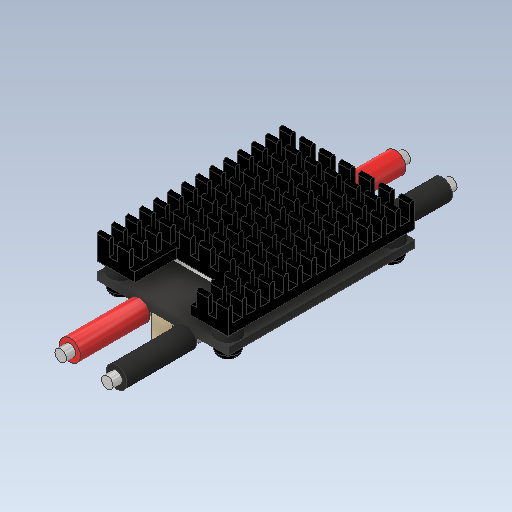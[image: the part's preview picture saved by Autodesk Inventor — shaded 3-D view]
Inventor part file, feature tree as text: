
AUTODESK INVENTOR PART (.ipt)
format: ipt  version: 2020.1 (Build 241239000, 239)  size: 1,061,888 bytes
history: native  units: mm
features: extrude x16, sketch x13, mirror x6, fillet x4, pattern_linear x2, plane x1, revolve x1, chamfer x1, emboss x1, projected_geometry x1
ambient origin geometry x8: Origin, YZ Plane, XZ Plane, XY Plane, X Axis, Y Axis, Z Axis, Center Point
bodies: Solid1 (feature_tree)
feature tree (46):
  extrude  "Extrusion1"  Depth=40.0mm
  extrude  "Extrusion2"  Depth=5.0mm
  extrude  "Extrusion3"  Depth=9.0mm
  extrude  "Extrusion4"  Depth=8.0mm
  extrude  "Extrusion5"  Depth=1.0mm TaperAngle=0.0deg
  fillet  "Fillet1"  Radius=0.2mm
  pattern_linear  "Rectangular Pattern1"  Count1=14 Spacing1=3.0mm
  mirror  "Mirror1"
  extrude  "Extrusion6"  Depth=1.0mm
  fillet  "Fillet2"  Radius=1.0mm
  pattern_linear  "Rectangular Pattern2"  Count1=11 Spacing1=3.0mm
  extrude  "Extrusion7"  Depth=0.1mm TaperAngle=0.0deg
  fillet  "Fillet3"  Radius=1.0mm
  extrude  "Extrusion8"  Depth=1.0mm
  mirror  "Mirror2"
  mirror  "Mirror3"
  sketch  "Sketch9"  dims[d19=0.5mm d20=140.0mm d22=3.0mm]
  extrude  "Extrusion9"  Depth=0.1mm
  fillet  "Fillet4"  Radius=1.0mm
  mirror  "Mirror4"
  plane  "Work Plane1"
  revolve  "Revolution1"  [1 undecoded]
  mirror  "Mirror5"
  mirror  "Mirror6"
  extrude  "Extrusion10"  Depth=0.1mm
  extrude  "Extrusion11"  Depth=0.1mm
  extrude  "Extrusion12"  Depth=0.1mm
  extrude  "Extrusion13"  Depth=0.1mm
  extrude  "Extrusion14"  Depth=0.1mm
  chamfer  "Chamfer1"  Distance=0.1mm
  extrude  "Extrusion15"  Depth=0.1mm
  extrude  "Extrusion16"  Depth=0.1mm TaperAngle=0.0deg
  emboss  "Emboss1"
  sketch  "Sketch1"  dims[d0=28.0mm d1=40.0mm]
  sketch  "Sketch2"  dims[d2=1.57mm d3=0.0mm d4=5.0mm]
  sketch  "Sketch3"  dims[d5=2.0mm d6=0.0mm d7=9.0mm]
  sketch  "Sketch4"  dims[d8=8.0mm d9=8.0mm]
  projected_geometry  "Projected Loop1"
  sketch  "Sketch5"  dims[d10=2.0mm d11=0.0mm d12=1.0mm d13=0.0mm d14=0.2mm]
  sketch  "Sketch6"  dims[d15=1.0mm]
  sketch  "Sketch7"  dims[d16=2.5mm]
  sketch  "Sketch8"  dims[d17=3.5mm d18=0.0mm]
  sketch  "Sketch10"  dims[d23=20.0mm d25=4.25mm d26=2.5mm d27=1.0mm]
  sketch  "Sketch11"  dims[d28=3.5mm d29=0.0mm]
  sketch  "Sketch12"  dims[d30=0.5mm d31=110.0mm d33=3.0mm d34=30.0mm d36=4.25mm]
  sketch  "Sketch13"  dims[d37=4.5mm d38=2.0mm d39=0.0mm d40=1.0mm d41=1.0mm d42=4.0mm d43=1.0mm d44=1.5mm d45=0.0mm d46=5.0mm d47=8.0mm d48=0.1mm d49=6.0mm d50=4.0mm d51=0.1mm d52=0.5mm d53=3.0mm d54=0.0mm d55=1.999992mm d59=1.24mm d60=2.0mm d61=20.0mm d62=90.0deg d63=2.25mm d64=0.5mm d65=1.0mm d66=1.0mm d67=0.5mm d68=0.5mm d70=0.3mm d71=0.5mm d72=0.5mm d73=0.5mm d74=0.5mm d75=1.48mm d76=1.0mm d77=0.0mm d78=6.0mm d79=0.0mm d80=4.0mm d81=0.0mm d82=1.5mm d83=0.0mm d84=5.0mm d85=0.0mm d86=0.2mm d87=2.0mm d88=45.0deg d89=0.5mm d90=0.5mm d91=1.0mm d92=6.0mm d93=0.0mm d94=1.0mm d95=2.0mm d97=0.5mm d98=2.0mm d99=6.0mm d100=0.0mm d101=1.0mm d102=3.0mm d103=3.0mm d105=0.1mm d106=0.0mm]
note: 1 required parameter value undecoded (feature->parameter linkage not recoverable at this tier; creation-order binding heuristic only, values carry confidence <= 0.55)
